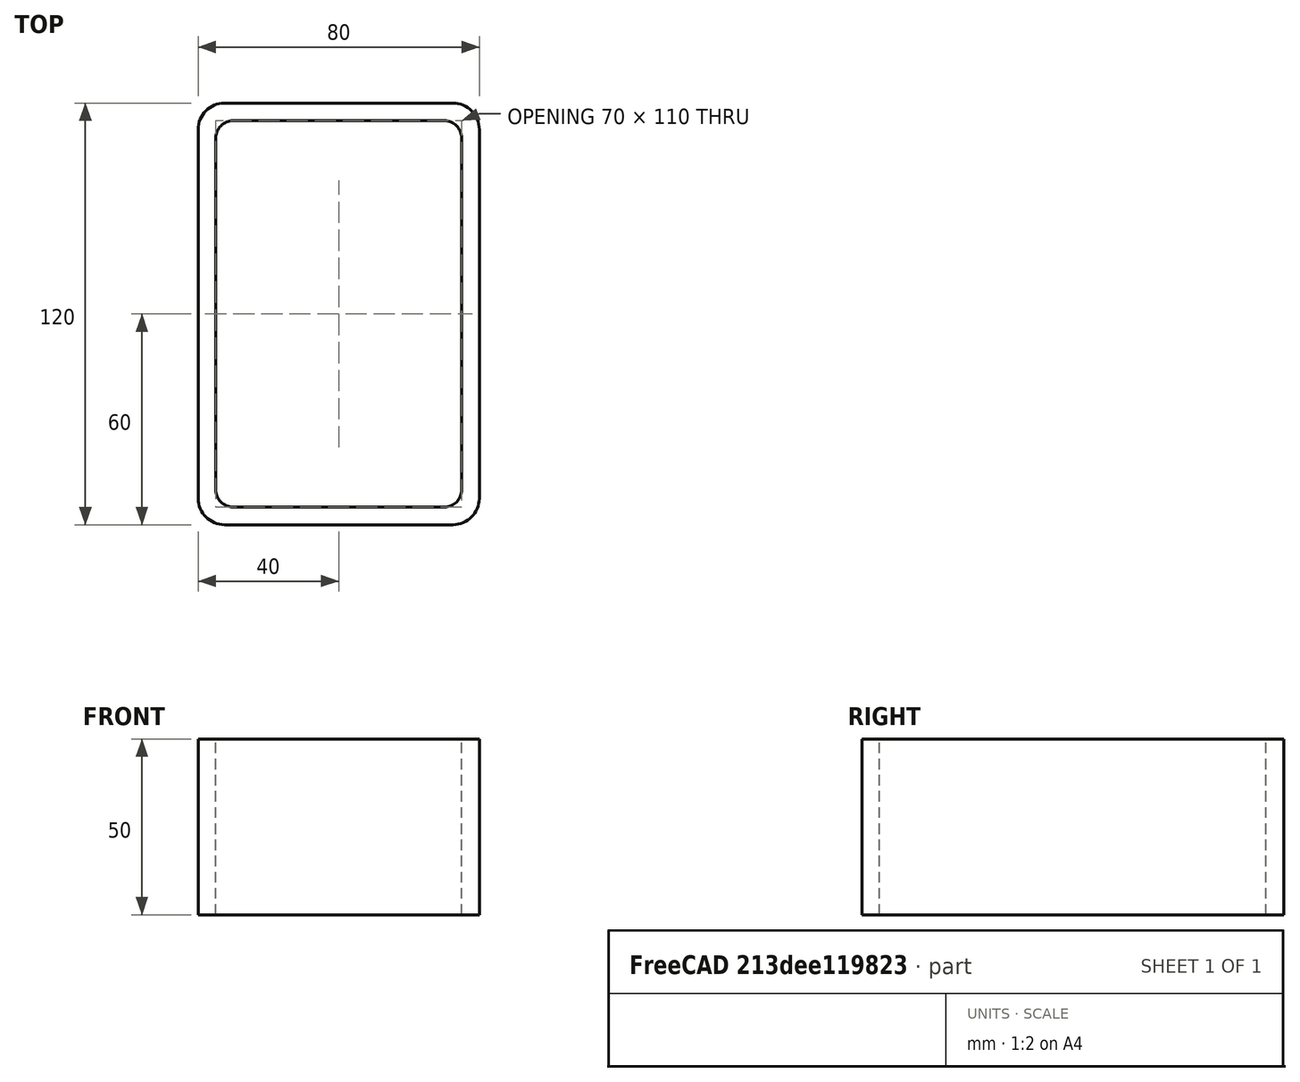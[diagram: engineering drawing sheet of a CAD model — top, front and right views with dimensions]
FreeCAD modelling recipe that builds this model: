
FCSTD DOCUMENT  (FreeCAD 0.15R4671 (Git))
Label: Rectangular hollow section 120x80x5 EN10219 S235JRH
License: All rights reserved
LicenseURL: http://en.wikipedia.org/wiki/All_rights_reserved
objects: Sketcher::SketchObject×1, Part::Extrusion×1
note: 2 computed .brp shape members not serialized (recipe doc carries the construction recipe); baked Part::Feature solids carry a one-line shape summary decoded from their .brp

FEATURE [Sketcher::SketchObject] Sketch
  sketch-geometry (16):
    g0: LineSegment StartX=-30 StartY=55 StartZ=0 EndX=30 EndY=55 EndZ=0
    g1: LineSegment StartX=35 StartY=50 StartZ=0 EndX=35 EndY=-50 EndZ=0
    g2: LineSegment StartX=30 StartY=-55 StartZ=0 EndX=-30 EndY=-55 EndZ=0
    g3: LineSegment StartX=-35 StartY=-50 StartZ=0 EndX=-35 EndY=50 EndZ=0
    g4: LineSegment StartX=-32.5 StartY=60 StartZ=0 EndX=32.5 EndY=60 EndZ=0
    g5: LineSegment StartX=40 StartY=52.5 StartZ=0 EndX=40 EndY=-52.5 EndZ=0
    g6: LineSegment StartX=32.5 StartY=-60 StartZ=0 EndX=-32.5 EndY=-60 EndZ=0
    g7: LineSegment StartX=-40 StartY=-52.5 StartZ=0 EndX=-40 EndY=52.5 EndZ=0
    g8: ArcOfCircle CenterX=-30 CenterY=50 CenterZ=0 NormalX=0 NormalY=0 NormalZ=1 Radius=5 StartAngle=1.5708 EndAngle=3.14159
    g9: ArcOfCircle CenterX=30 CenterY=50 CenterZ=0 NormalX=0 NormalY=0 NormalZ=1 Radius=5 StartAngle=0 EndAngle=1.5708
    g10: ArcOfCircle CenterX=30 CenterY=-50 CenterZ=0 NormalX=0 NormalY=0 NormalZ=1 Radius=5 StartAngle=4.71239 EndAngle=6.28319
    g11: ArcOfCircle CenterX=-30 CenterY=-50 CenterZ=0 NormalX=0 NormalY=0 NormalZ=1 Radius=5 StartAngle=3.14159 EndAngle=4.71239
    g12: ArcOfCircle CenterX=32.5 CenterY=52.5 CenterZ=0 NormalX=0 NormalY=0 NormalZ=1 Radius=7.5 StartAngle=0 EndAngle=1.5708
    g13: ArcOfCircle CenterX=32.5 CenterY=-52.5 CenterZ=0 NormalX=0 NormalY=0 NormalZ=1 Radius=7.5 StartAngle=4.71239 EndAngle=6.28319
    g14: ArcOfCircle CenterX=-32.5 CenterY=-52.5 CenterZ=0 NormalX=0 NormalY=0 NormalZ=1 Radius=7.5 StartAngle=3.14159 EndAngle=4.71239
    g15: ArcOfCircle CenterX=-32.5 CenterY=52.5 CenterZ=0 NormalX=0 NormalY=0 NormalZ=1 Radius=7.5 StartAngle=1.5708 EndAngle=3.14159
  constraints (36):
    c: Horizontal(g2)
    c: Vertical(g3)
    c: Horizontal(g6)
    c: Vertical(g7)
    c: Tangent(g3,g8) = 1.5708
    c: Tangent(g0,g8) = 1.5708
    c: Tangent(g0,g9) = 1.5708
    c: Tangent(g1,g9) = 1.5708
    c: Tangent(g1,g10) = 1.5708
    c: Tangent(g2,g10) = 1.5708
    c: Tangent(g2,g11) = 1.5708
    c: Tangent(g3,g11) = 1.5708
    c: Tangent(g4,g12) = 1.5708
    c: Tangent(g5,g12) = 1.5708
    c: Tangent(g5,g13) = 1.5708
    c: Tangent(g6,g13) = 1.5708
    c: Tangent(g6,g14) = 1.5708
    c: Tangent(g7,g14) = 1.5708
    c: Tangent(g7,g15) = 1.5708
    c: Tangent(g4,g15) = 1.5708
    c: Equal(g9,g8)
    c: Equal(g9,g11)
    c: Equal(g9,g10)
    c: Equal(g12,g15)
    c: Equal(g12,g14)
    c: Equal(g12,g13)
    c: Symmetric(g4,g6,g-1)
    c: Symmetric(g7,g5,g-2)
    c: DistanceY(g4,g6) = -120
    c: DistanceX(g7,g5) = 80
    c: Symmetric(g3,g1,g-2)
    c: Symmetric(g0,g2,g-1)
    c: DistanceY(g0,g4) = 5
    c: DistanceX(g5,g1) = -5
    c: Radius(g9) = 5
    c: Radius(g12) = 7.5
FEATURE [Part::Extrusion] Extrude  label="Rectangular hollow section 120x80x5 EN10219 S235JRH"
  Base = -> Sketch
  Dir = (0,0,50)
  Solid = true
